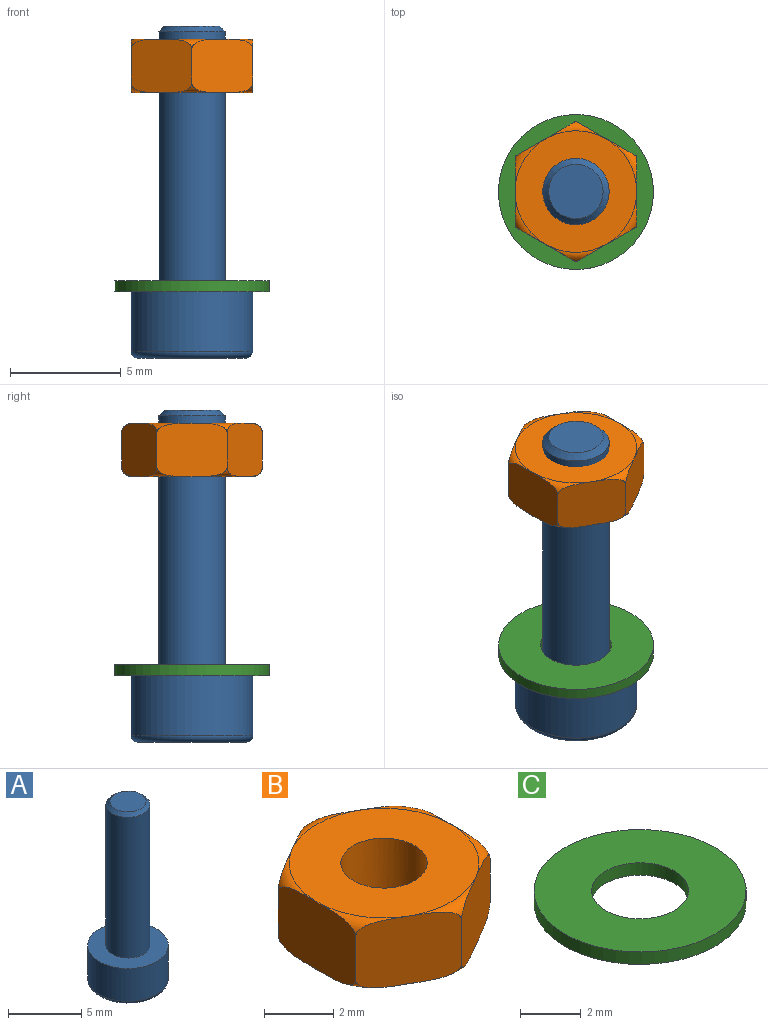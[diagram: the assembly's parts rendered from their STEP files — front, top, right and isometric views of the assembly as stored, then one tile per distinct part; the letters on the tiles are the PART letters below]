
ASSEMBLY  parts=3 mates=3
PART A: 14 faces, bbox 6x6x15 mm
  f0: plane 4.95x4.95mm, normal (0,0,-1), area 13.5mm2, adj f3,f4,f5,f6,f7,f8,f9
  f1: cylinder r=2.75mm len=5.5mm, axis (0,0,1), area 47.1mm2, adj f2,f3
  f2: plane 5.5x5.5mm, normal (0,0,1), area 16.7mm2, adj f1,f11
  f3: torus R=2.48mm, axis (0,0,-1), area 7.2mm2, adj f0,f1
  f4: plane 1.5x1.49mm, normal (-1,0,0), area 2.2mm2, adj f0,f5,f9,f10
  f5: plane 1.5x1.29mm, normal (-0.5,-0.87,0), area 2.2mm2, adj f0,f4,f6,f10
  f6: plane 1.5x1.29mm, normal (0.5,-0.87,0), area 2.2mm2, adj f0,f5,f7,f10
  f7: plane 1.5x1.49mm, normal (1,0,0), area 2.2mm2, adj f0,f6,f8,f10
  f8: plane 1.5x1.29mm, normal (0.5,0.87,0), area 2.2mm2, adj f0,f7,f9,f10
  f9: plane 1.5x1.29mm, normal (-0.5,0.87,0), area 2.2mm2, adj f0,f4,f8,f10
  f10: plane 2.98x2.58mm, normal (0,0,-1), area 5.8mm2, adj f4,f5,f6,f7,f8,f9
  f11: cylinder r=1.5mm len=11.73mm, axis (0,0,-1), area 110.5mm2, adj f2,f13
  f12: plane 2.46x2.46mm, normal (0,0,1), area 4.7mm2, adj f13
  f13: cone r=1.23mm half-angle=45deg, axis (0,0,-1), area 3.3mm2, adj f11,f12
PART B: 11 faces, bbox 6.9x6.9x2.4 mm
  f0: plane 5.49x5.49mm, normal (0,0,1), area 18.8mm2, adj f1,f10
  f1: torus R=2.75mm, axis (0,0,-1), area 2.8mm2, adj f0,f2,f3,f4,f5,f6,f7
  f2: plane 2.75x2.4mm, normal (0.5,0.87,0), area 7.3mm2, adj f1,f3,f7,f9
  f3: plane 3.18x2.4mm, normal (1,0,0), area 7.3mm2, adj f1,f2,f4,f9
  f4: plane 2.75x2.4mm, normal (0.5,-0.87,0), area 7.3mm2, adj f1,f3,f5,f9
  f5: plane 2.75x2.4mm, normal (-0.5,-0.87,0), area 7.3mm2, adj f1,f4,f6,f9
  f6: plane 3.18x2.4mm, normal (-1,0,0), area 7.3mm2, adj f1,f5,f7,f9
  f7: plane 2.75x2.4mm, normal (-0.5,0.87,0), area 7.3mm2, adj f1,f2,f6,f9
  f8: plane 5.49x5.49mm, normal (0,0,-1), area 18.8mm2, adj f9,f10
  f9: torus R=2.75mm, axis (0,0,-1), area 2.8mm2, adj f2,f3,f4,f5,f6,f7,f8
  f10: cylinder r=1.25mm len=2.5mm, axis (0,0,-1), area 18.8mm2, adj f0,f8
PART C: 4 faces, bbox 7x7x0.5 mm
  f0: cylinder r=1.6mm len=3.2mm, axis (0,0,-1), area 5mm2, adj f2,f3
  f1: cylinder r=3.5mm len=7mm, axis (0,0,-1), area 11mm2, adj f2,f3
  f2: plane 7x7mm, normal (0,0,1), area 30.4mm2, adj f0,f1
  f3: plane 7x7mm, normal (0,0,-1), area 30.4mm2, adj f0,f1
PLACE A t=(-67.9,93.84,7.78)mm
PLACE B t=(-47.9,113.84,16.77)mm
PLACE C t=(-17.9,103.84,7.78)mm
MATE cylindrical A.f1 <-> C.f0  axis (0,0,-1) through (-27.9,93.84,13.64)mm
MATE planar C.f0 <-> A.f1  axis (0,0,-1) through (-27.9,93.84,7.78)mm
MATE cylindrical B.f1 <-> C.f0  axis (0,0,-1) through (-27.9,93.84,17.97)mm
